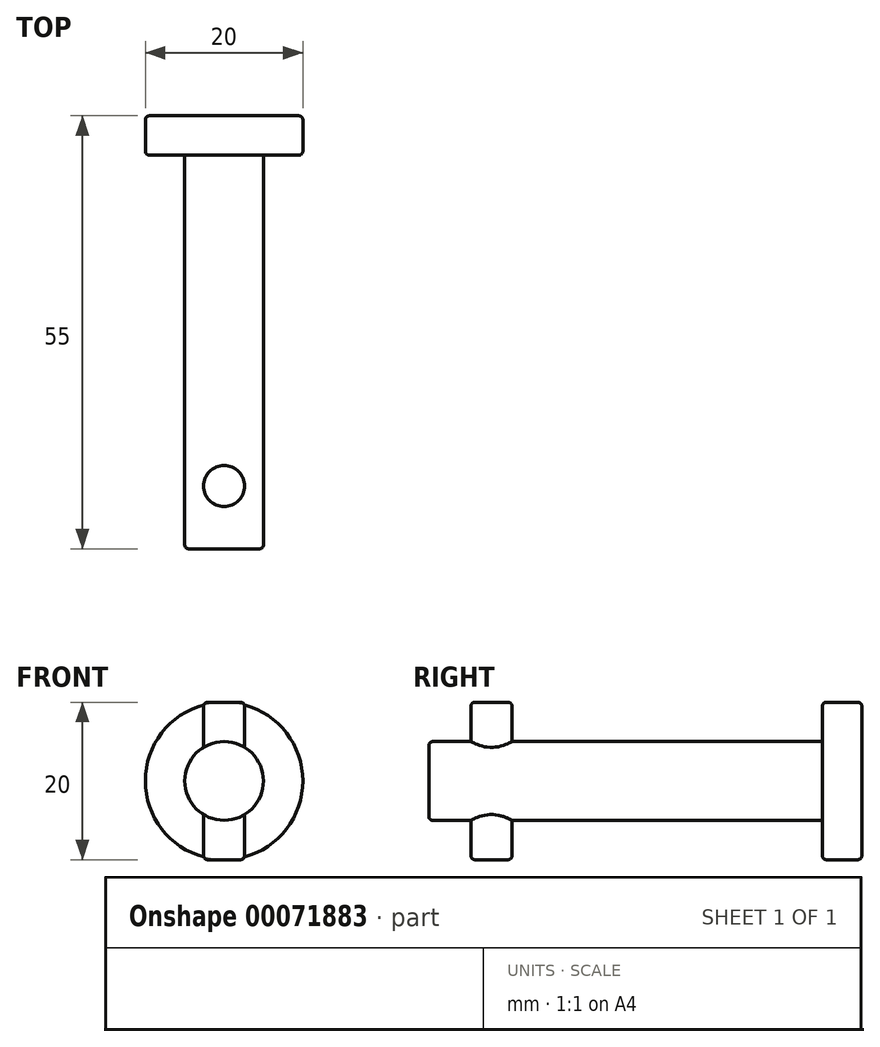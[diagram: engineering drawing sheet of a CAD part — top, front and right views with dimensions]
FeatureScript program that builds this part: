
annotation { "Feature Type Name" : "Feature", "Feature Type Description" : "" }
export const myFeature = defineFeature(function(context is Context, id is Id, definition is map)
    precondition{}
    {
        {
            var Q0;
            Q0=qCreatedBy(makeId("Front.planeOp"),FACE);
            var sketch = newSketch(context, id + "F0", { "sketchPlane" : qUnion([Q0])});
            skCircle(sketch, "E0", {"center": v(0, 0) * mm, "radius": 10 * mm});
            skSolve(sketch);
        }
        {
            var Q0;
            Q0=makeQuery(id+"F0.imprint","IMPRINT",FACE,{"disambiguationData":[TD([[makeQuery(id+"F0.imprint","IMPRINT",EDGE,{"derivedFrom":sQuery(id+"F0.wireOp",EDGE,"E0")}),1.0]])]});
            extrude(context, id + "F1", {"entities" : qUnion([Q0]), "depth" : 5 * mm});
        }
        {
            var Q0;
            Q0=makeQuery(id+"F1.opExtrude","CAP_FACE",FACE,{"disambiguationData":[OSD([sQuery(id+"F0.wireOp",EDGE,"E0")])],"isStart":false});
            var sketch = newSketch(context, id + "F2", { "sketchPlane" : qUnion([Q0])});
            skCircle(sketch, "E1", {"center": v(0, 0) * mm, "radius": 5 * mm});
            skSolve(sketch);
        }
        {
            var Q0;
            Q0 = qSketchRegion(id + "F2", true);
            extrude(context, id + "F3", {"entities" : qUnion([Q0]), "operationType" : NewBodyOperationType.ADD, "depth" : 50 * mm});
        }
        {
            var Q0;
            Q0=makeQuery(id+"F1.opExtrude","CAP_EDGE",EDGE,{"disambiguationData":[OSD([sQuery(id+"F0.wireOp",EDGE,"E0")])],"isStart":false});
            var Q1;
            Q1=makeQuery(id+"F1.opExtrude","CAP_EDGE",EDGE,{"disambiguationData":[OSD([sQuery(id+"F0.wireOp",EDGE,"E0")])],"isStart":true});
            var Q2;
            Q2=makeQuery(id+"F3.opExtrude","CAP_EDGE",EDGE,{"disambiguationData":[OSD([sQuery(id+"F2.wireOp",EDGE,"E1")])],"isStart":true});
            var Q3;
            Q3=makeQuery(id+"F3.opExtrude","CAP_EDGE",EDGE,{"disambiguationData":[OSD([sQuery(id+"F2.wireOp",EDGE,"E1")])],"isStart":false});
            fillet(context, id + "F4", {"entities" : qUnion([Q0, Q1, Q2, Q3]), "radius" : .5 * mm, "tangentPropagation" : true, "allowEdgeOverflow" : false});
        }
        {
            var Q0;
            Q0=qCreatedBy(makeId("Top.planeOp"),FACE);
            var sketch = newSketch(context, id + "F5", { "sketchPlane" : qUnion([Q0])});
            skCircle(sketch, "E2", {"center": v(0, -47.04) * mm, "radius": 2.6 * mm});
            skSolve(sketch);
        }
        {
            var Q0;
            Q0 = qSketchRegion(id + "F5", true);
            extrude(context, id + "F6", {"entities" : qUnion([Q0]), "operationType" : NewBodyOperationType.ADD, "depth" : 10 * mm, "hasSecondDirection" : true, "secondDirectionOppositeDirection" : true, "secondDirectionDepth" : 10 * mm});
        }
        {
            var Q0;
            Q0=makeQuery(id+"F6.opExtrude","CAP_EDGE",EDGE,{"disambiguationData":[OSD([sQuery(id+"F5.wireOp",EDGE,"E2")])],"isStart":false});
            var Q1;
            Q1=makeQuery(id+"F6.opExtrude","CAP_EDGE",EDGE,{"disambiguationData":[OSD([sQuery(id+"F5.wireOp",EDGE,"E2")])],"isStart":true});
            fillet(context, id + "F7", {"entities" : qUnion([Q0, Q1]), "radius" : .5 * mm, "tangentPropagation" : true, "allowEdgeOverflow" : false});
        }
    });
